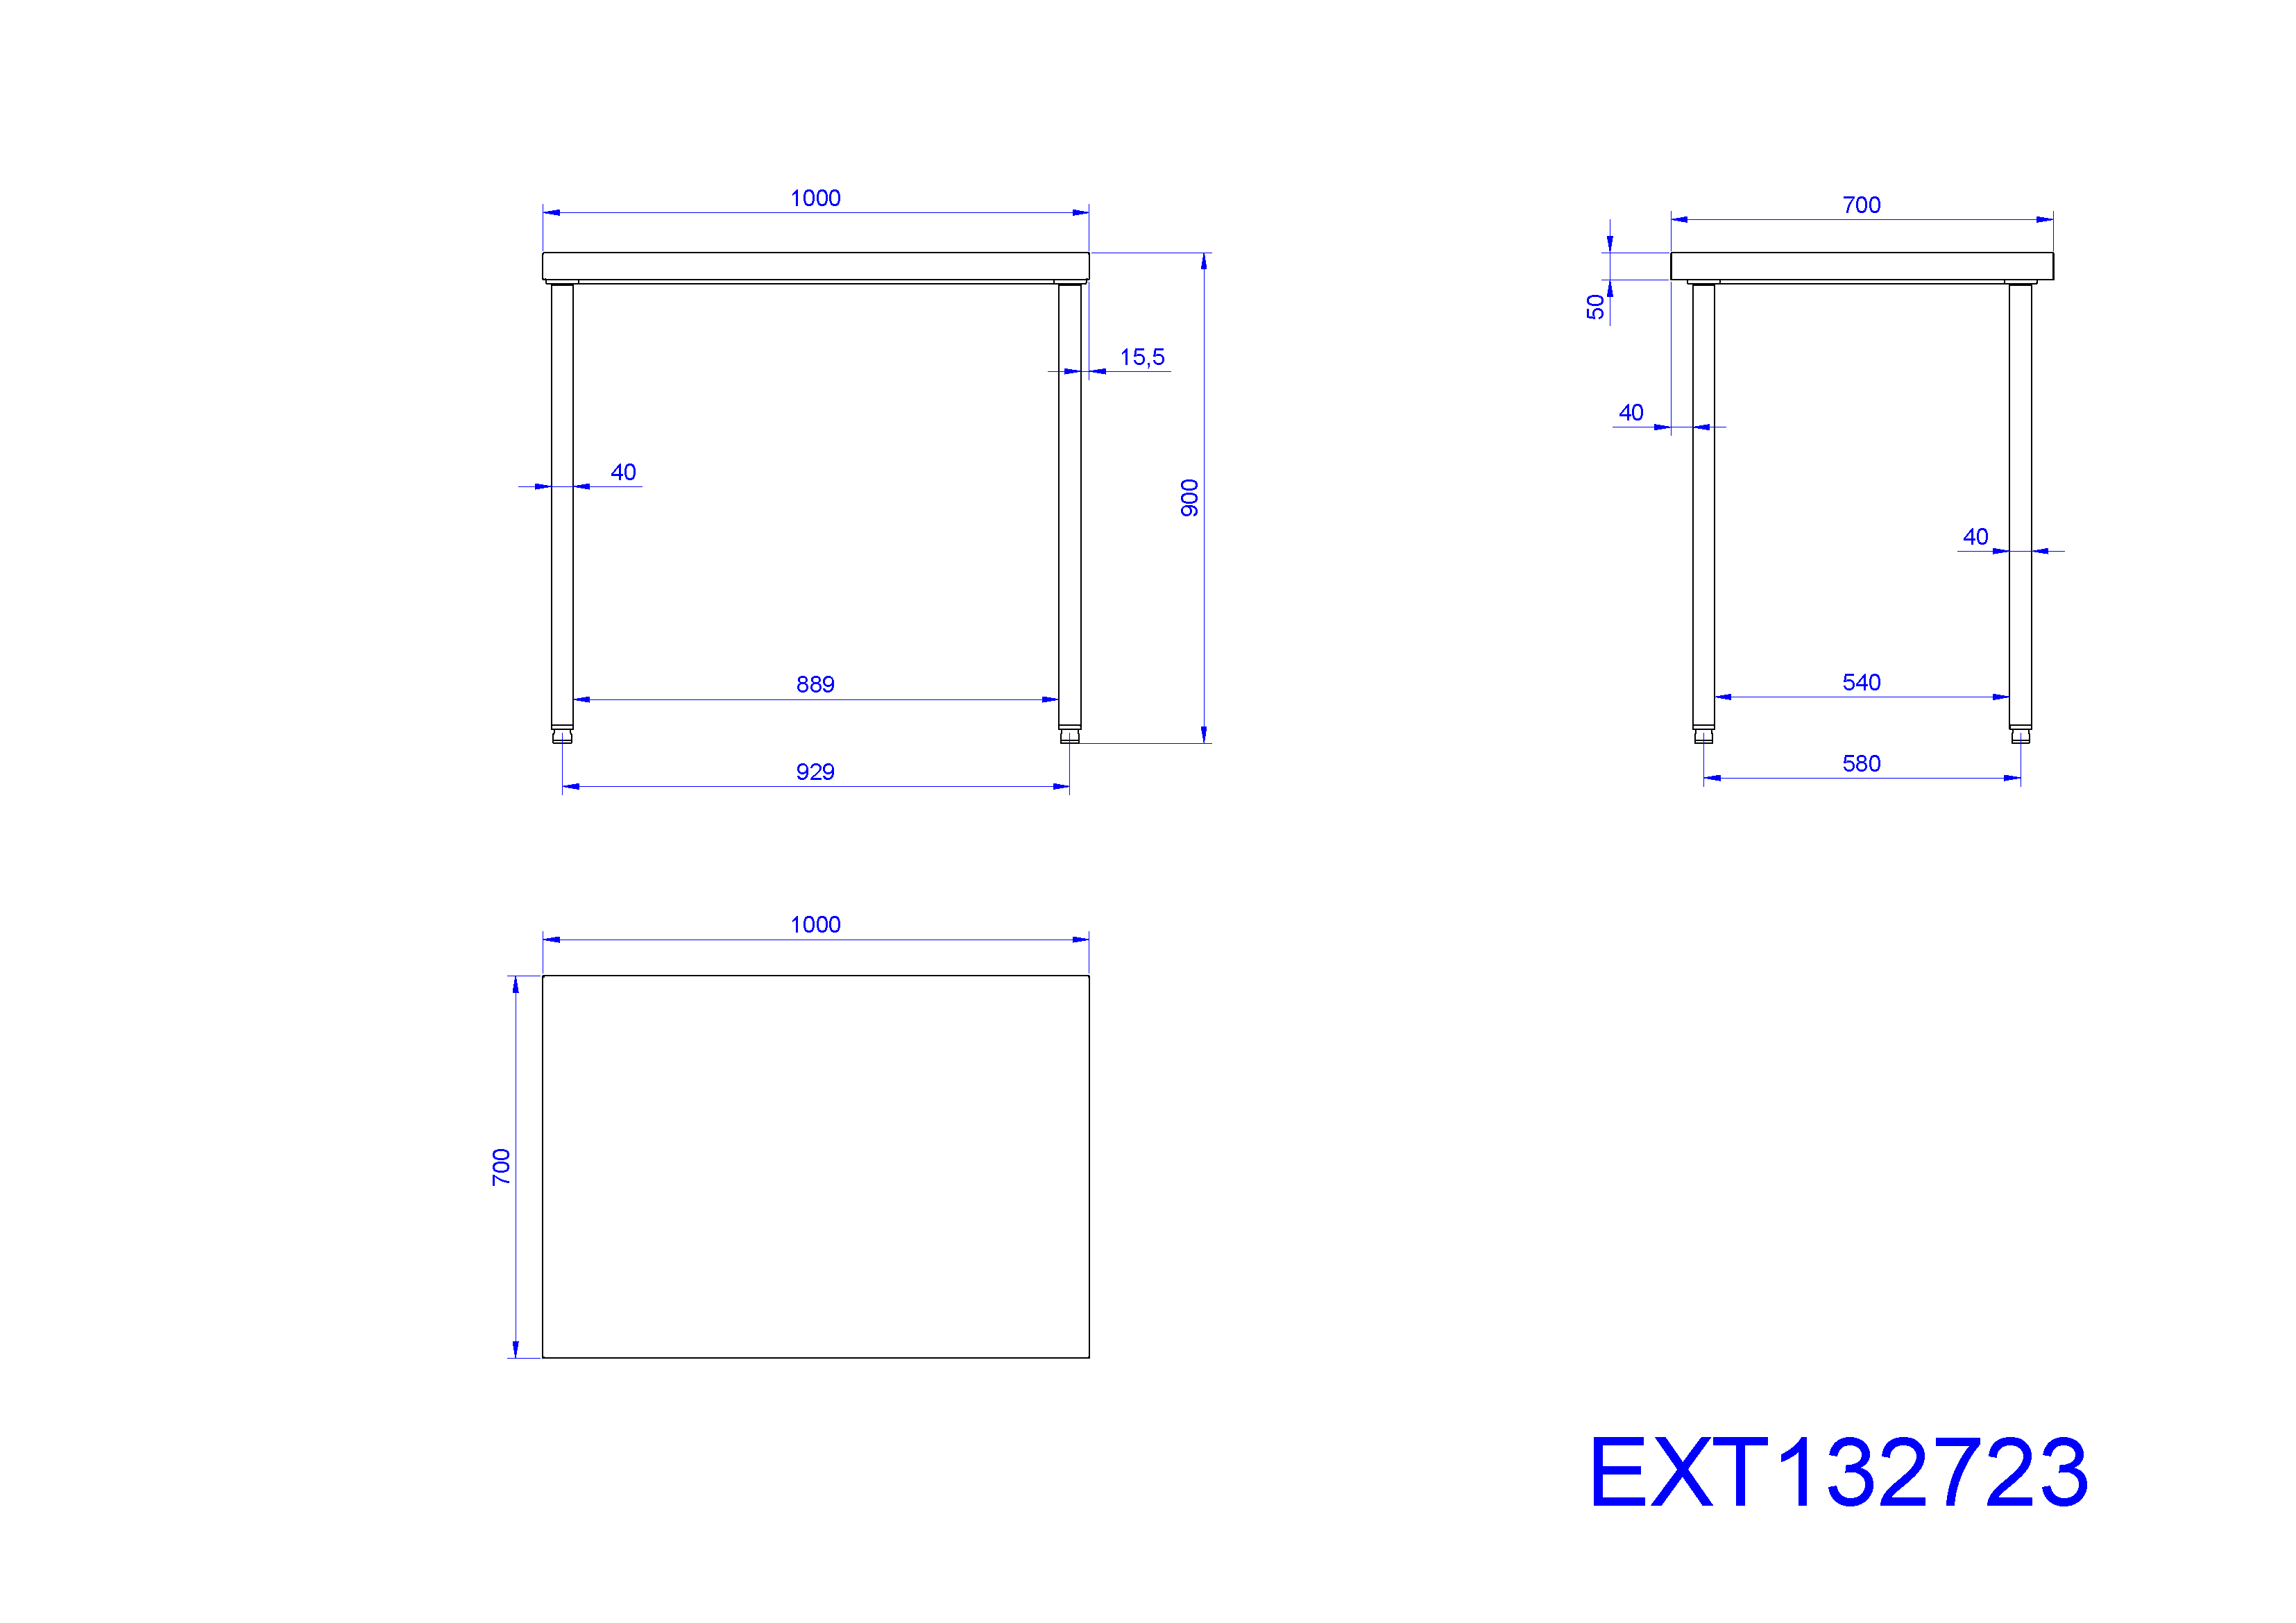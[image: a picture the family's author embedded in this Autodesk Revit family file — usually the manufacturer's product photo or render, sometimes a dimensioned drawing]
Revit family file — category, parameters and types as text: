
# Revit family: QF_ZANUSSI_132727_TG1800PN
name_source: partatom
category: Attrezzature speciali
units: mm (PartAtom-declared; Revit-internal decimal feet)

## family parameters
Basato su piano di lavoro = No
Condiviso = No
Punto di calcolo locali = No
Quota connettore circolare = Usa diametro
Sempre verticale = Sì
Taglio con vuoti quando caricato = No
Tipo di parte = Normale

## types (1)
- Standard
    Accessory = Sì
    Cold Water Size = 0 mm
    Compressed Air Pressure = 0.0 Pa
    Compressed Air Size = 0 mm
    Compressed Air Volume = 0.0 L/s
    Condensate Return Size = 0 mm
    Cycle = 0 Hz
    Depth Actual = 700 mm  [stored 2.29659 ft]
    Descrizione = WORK TABLE 1800 MM
    Direct Waste Size = 0 mm
    Gas Input Pressure = 0
    Gas KW = 0
    Gas Size = 0 mm
    HP = 0 HP
    Height Actual = 900 mm  [stored 2.95276 ft]
    Hot Water Size = 0 mm
    Item Number = 132727
    Length Actual = 1800 mm  [stored 5.90551 ft]
    Modello = TG1800PN
    Phase = 0
    Produttore = Zanussi
    Prospetto di default = 0 mm  [stored 0 ft]
    Refrigerant Compressor Remote = Sì
    Refrigeration Liquid Line Size = 0 mm  [stored 0 ft]
    Refrigeration Suction Line Size = 0 mm  [stored 0 ft]
    Steam Consumption per Hour = 0
    Steam Supply Maximum Pressure = 0.0 Pa
    Steam Supply Minimum Pressure = 0.0 Pa
    Steam Supply Size = 0 mm
    URL = http://www.zanussiprofessional.com
    URL Manufacturer = http://www.zanussiprofessional.com
    Volts = 0 V
    Watts = 0 W
    Weight = 54.00 kg

note: source unit labels omitted for Gas Input Pressure — the stored unit's dimension contradicts the parameter name (converter mislabeling)

note: [stored X ft] marks values corroborated as IEEE doubles in the binary element streams (Revit-internal decimal feet)

## geometry (parser evidence)
native form markers: Sweep x2
no freeform markers — native parametric forms only
